# Revit family: Sanitary_Showers_hansgrohe_71761XXX-Talis-E-Single-lever-shower-mix5
name_source: partatom
category: Plumbing Fixtures
revit_build: Autodesk Revit 2018 (Build: 20170223_1515(x64)
units: mm (PartAtom-declared; Revit-internal decimal feet)

## family parameters
Always vertical = No
Cut with Voids When Loaded = No
OmniClass Number = 23.31.17.00
Part Type = Normal
Room Calculation Point = No
Round Connector Dimension = Use Diameter
Shared = No
Work Plane-Based = Yes

## types (1)
- 000 Chrome
    Always visible = Yes
    BIMobject category = Showers
    Default Elevation = 4' - 0"
    Design country = Germany
    EAN code = 4011097770901
    Edition number = 1
    GTIN code = https://4011097770901
    IFC Classification = Sanitary Terminal
    Installation instructions = https://www.hansgrohe.com
    Manufacturer country = Germany
    Manufacturer name = hansgrohe
    Material 1 = Hansgrohe - Metal - 000 Chrome
    OmniClass Code = 23-31 17 00
    OmniClass Description = Showers
    Product Guid = 2d539c6d-b8dc-441e-acb6-fb57d2aab9ed
    Product SKU = 71761XXX
    Product data url = https://www.bimobject.com
    Product family = Talis E
    Product group = Shower mixers
    Product name = 71761XXX Talis E Single lever shower mixer for exposed installation with centre distance 15.3 cm CH
    Product url = https://www.hansgrohe.com
    QR code = https://www.bimobject.com
    Technical description = https://www.hansgrohe.com
    UNSPSC Code = 30181503
    Uniclass 1.4 Code = L7214
    Uniclass 1.4 Description = Showers
    Weight Net (Kg) = 1.3

## geometry (parser evidence)
native form markers: Sweep x3
no freeform markers — native parametric forms only
